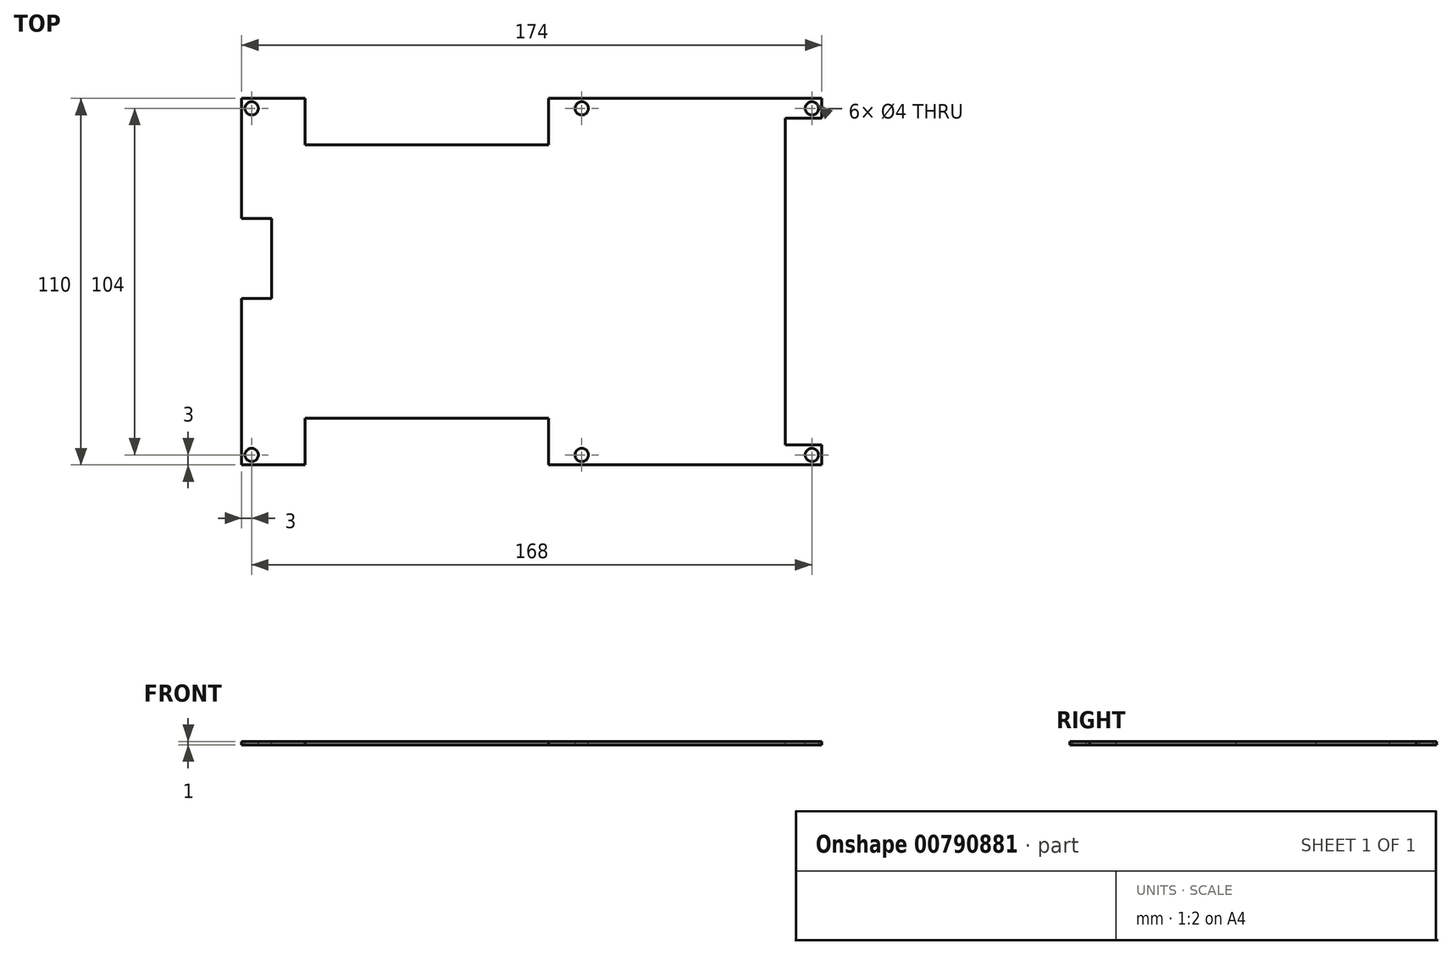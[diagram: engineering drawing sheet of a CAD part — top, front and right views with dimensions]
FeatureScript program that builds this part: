
annotation { "Feature Type Name" : "Feature", "Feature Type Description" : "" }
export const myFeature = defineFeature(function(context is Context, id is Id, definition is map)
    precondition{}
    {
        {
            assignVariable(context, id + "F0", {"name" : "T", "anyValue" : 1});
        }
        {
            var Q0;
            Q0=qCreatedBy(makeId("Top.planeOp"),FACE);
            var sketch = newSketch(context, id + "F1", { "sketchPlane" : qUnion([Q0])});
            skLineSegment(sketch, "E0.bottom", {"start": v(-87, -55) * mm, "end": v(87, -55) * mm});
            skLineSegment(sketch, "E0.top", {"start": v(-87, 55) * mm, "end": v(87, 55) * mm});
            skLineSegment(sketch, "E0.left", {"start": v(-87, -55) * mm, "end": v(-87, 55) * mm});
            skLineSegment(sketch, "E0.right", {"start": v(87, -55) * mm, "end": v(87, 55) * mm});
            skPoint(sketch, "E0.middle", {"position": v(0, 0) * mm});
            skSolve(sketch);
        }
        {
            var Q0;
            Q0 = qSketchRegion(id + "F1", true);
            extrude(context, id + "F2", {"entities" : qUnion([Q0]), "depth" : (getVariable(context, 'T')) * mm, "offsetDistance" : 25 * mm});
        }
        {
            var Q0;
            Q0=makeQuery(id+"F2.opExtrude","CAP_FACE",FACE,{"disambiguationData":[OSD([sQuery(id+"F1.wireOp",EDGE,"E0.bottom"),sQuery(id+"F1.wireOp",EDGE,"E0.top"),sQuery(id+"F1.wireOp",EDGE,"E0.left"),sQuery(id+"F1.wireOp",EDGE,"E0.right")])],"isStart":false});
            var sketch = newSketch(context, id + "F3", { "sketchPlane" : qUnion([Q0])});
            skLineSegment(sketch, "E1.bottom", {"start": v(-68, 55) * mm, "end": v(5, 55) * mm});
            skLineSegment(sketch, "E1.top", {"start": v(-68, 41) * mm, "end": v(5, 41) * mm});
            skLineSegment(sketch, "E1.left", {"start": v(-68, 55) * mm, "end": v(-68, 41) * mm});
            skLineSegment(sketch, "E1.right", {"start": v(5, 55) * mm, "end": v(5, 41) * mm});
            skLineSegment(sketch, "E2.MirrorCS", {"start": v(5, -55) * mm, "end": v(5, -41) * mm});
            skLineSegment(sketch, "E3.MirrorCS", {"start": v(-68, -41) * mm, "end": v(5, -41) * mm});
            skLineSegment(sketch, "E4.MirrorCS", {"start": v(-68, -55) * mm, "end": v(-68, -41) * mm});
            skLineSegment(sketch, "E5.MirrorCS", {"start": v(-68, -55) * mm, "end": v(5, -55) * mm});
            skLineSegment(sketch, "E6.bottom", {"start": v(-87, -5) * mm, "end": v(-78, -5) * mm});
            skLineSegment(sketch, "E6.top", {"start": v(-87, 19) * mm, "end": v(-78, 19) * mm});
            skLineSegment(sketch, "E6.left", {"start": v(-87, -5) * mm, "end": v(-87, 19) * mm});
            skLineSegment(sketch, "E6.right", {"start": v(-78, -5) * mm, "end": v(-78, 19) * mm});
            skLineSegment(sketch, "E7.bottom", {"start": v(87, 49) * mm, "end": v(76, 49) * mm});
            skLineSegment(sketch, "E7.top", {"start": v(87, -49) * mm, "end": v(76, -49) * mm});
            skLineSegment(sketch, "E7.left", {"start": v(87, 49) * mm, "end": v(87, -49) * mm});
            skLineSegment(sketch, "E7.right", {"start": v(76, 49) * mm, "end": v(76, -49) * mm});
            skSolve(sketch);
        }
        {
            var Q0;
            Q0 = qSketchRegion(id + "F3", true);
            extrude(context, id + "F4", {"entities" : qUnion([Q0]), "operationType" : NewBodyOperationType.REMOVE, "oppositeDirection" : true, "depth" : 25 * mm, "offsetDistance" : 25 * mm});
        }
        {
            var Q0;
            Q0=makeQuery(id+"F2.opExtrude","CAP_FACE",FACE,{"disambiguationData":[OSD([sQuery(id+"F1.wireOp",EDGE,"E0.bottom"),sQuery(id+"F1.wireOp",EDGE,"E0.top"),sQuery(id+"F1.wireOp",EDGE,"E0.left"),sQuery(id+"F1.wireOp",EDGE,"E0.right")])],"isStart":false});
            var sketch = newSketch(context, id + "F5", { "sketchPlane" : qUnion([Q0])});
            skPoint(sketch, "E8", {"position": v(-84, 52) * mm});
            skPoint(sketch, "E9", {"position": v(-84, -52) * mm});
            skPoint(sketch, "E10", {"position": v(15, -52) * mm});
            skPoint(sketch, "E11", {"position": v(84, -52) * mm});
            skPoint(sketch, "E12", {"position": v(84, 52) * mm});
            skPoint(sketch, "E13", {"position": v(15, 52) * mm});
            skSolve(sketch);
        }
        {
            var Q0;
            Q0=sQuery(id+"F5.wireOp",VERTEX,"E8");
            var Q1;
            Q1=sQuery(id+"F5.wireOp",VERTEX,"E10");
            var Q2;
            Q2=sQuery(id+"F5.wireOp",VERTEX,"E13");
            var Q3;
            Q3=sQuery(id+"F5.wireOp",VERTEX,"E12");
            var Q4;
            Q4=sQuery(id+"F5.wireOp",VERTEX,"E11");
            var Q5;
            Q5=sQuery(id+"F5.wireOp",VERTEX,"E9");
            var Q6;
            Q6=makeQuery(id+"F2.opExtrude","SWEPT_BODY",BODY,{"disambiguationData":[OSD([sQuery(id+"F1.wireOp",EDGE,"E0.bottom"),sQuery(id+"F1.wireOp",EDGE,"E0.top"),sQuery(id+"F1.wireOp",EDGE,"E0.left"),sQuery(id+"F1.wireOp",EDGE,"E0.right")])]});
            hole(context, id + "F6", {"style" : HoleStyle.SIMPLE, "endStyle" : HoleEndStyle.THROUGH, "holeDiameter" : 4 * mm, "majorDiameter" : 5 * mm, "isTappedThrough" : true, "tappedDepth" : 12 * mm, "tapClearance" : 3, "locations" : qUnion([Q0, Q1, Q2, Q3, Q4, Q5]), "scope" : qUnion([Q6])});
        }
    });
